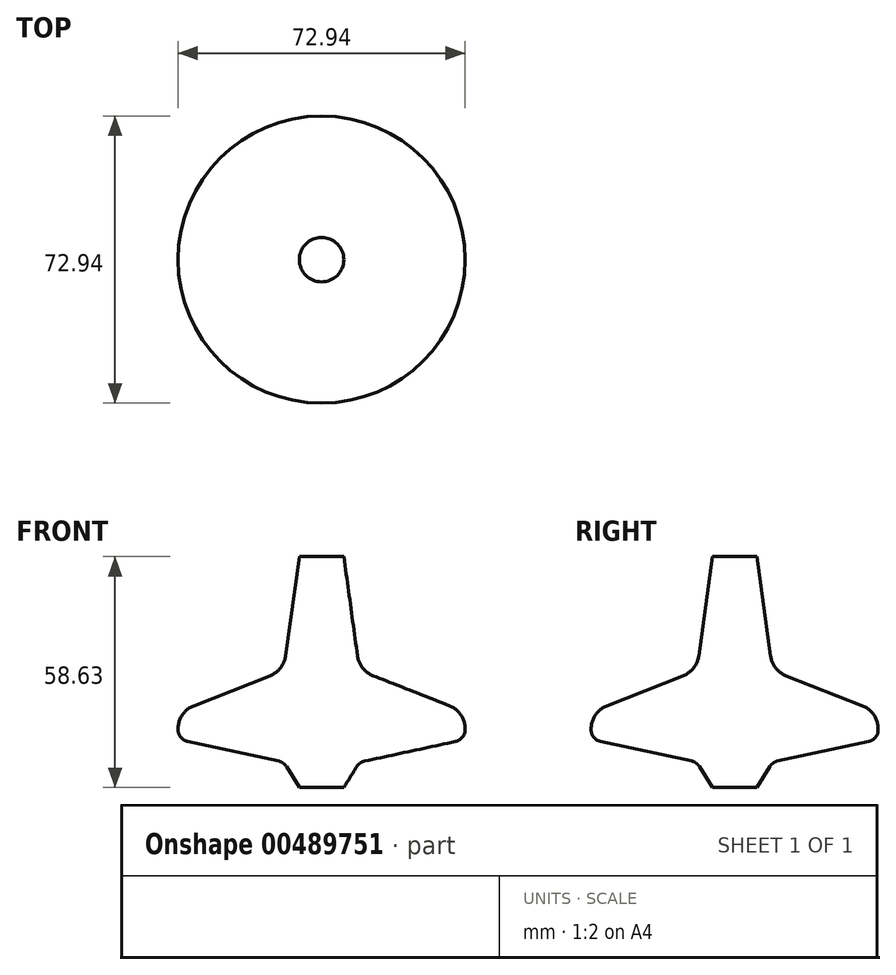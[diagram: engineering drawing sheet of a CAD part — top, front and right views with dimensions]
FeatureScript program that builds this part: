
annotation { "Feature Type Name" : "Feature", "Feature Type Description" : "" }
export const myFeature = defineFeature(function(context is Context, id is Id, definition is map)
    precondition{}
    {
        {
            var Q0;
            Q0=qCreatedBy(makeId("Front.planeOp"),FACE);
            var sketch = newSketch(context, id + "F0", { "sketchPlane" : qUnion([Q0])});
            skLineSegment(sketch, "E0", {"start": v(0, 0) * mm, "end": v(5.66, 0) * mm});
            skLineSegment(sketch, "E1", {"start": v(5.66, 0) * mm, "end": v(8.95, 5.3) * mm});
            skLineSegment(sketch, "E2", {"start": v(10.9, 6.68) * mm, "end": v(34.05, 11.67) * mm});
            skLineSegment(sketch, "E3", {"start": v(36.47, 14.66) * mm, "end": v(36.47, 14.86) * mm});
            skLineSegment(sketch, "E4", {"start": v(32.44, 20.77) * mm, "end": v(13.1, 28.4) * mm});
            skLineSegment(sketch, "E5", {"start": v(9.13, 33.43) * mm, "end": v(5.66, 58.63) * mm});
            skLineSegment(sketch, "E6", {"start": v(5.66, 58.63) * mm, "end": v(0, 58.63) * mm});
            skLineSegment(sketch, "E7", {"start": v(0, 58.63) * mm, "end": v(0, 0) * mm});
            skPoint(sketch, "E8.visualSharp", {"position": v(9.63, 29.75) * mm});
            skArc(sketch, "E8.filletArc", {"start": v(9.13, 33.43) * mm, "mid": v(10.43, 30.37) * mm, "end": v(13.1, 28.4) * mm});
            skPoint(sketch, "E9.visualSharp", {"position": v(36.47, 19.19) * mm});
            skArc(sketch, "E9.filletArc", {"start": v(36.47, 14.86) * mm, "mid": v(35.37, 18.44) * mm, "end": v(32.44, 20.77) * mm});
            skPoint(sketch, "E10.visualSharp", {"position": v(36.47, 12.2) * mm});
            skArc(sketch, "E10.filletArc", {"start": v(34.05, 11.67) * mm, "mid": v(35.79, 12.74) * mm, "end": v(36.47, 14.66) * mm});
            skPoint(sketch, "E11.visualSharp", {"position": v(9.63, 6.4) * mm});
            skArc(sketch, "E11.filletArc", {"start": v(10.9, 6.68) * mm, "mid": v(9.79, 6.19) * mm, "end": v(8.95, 5.3) * mm});
            skSolve(sketch);
        }
        {
            var Q0;
            Q0=makeQuery(id+"F0.imprint","IMPRINT",FACE,{"disambiguationData":[TD([[makeQuery(id+"F0.imprint","IMPRINT",EDGE,{"derivedFrom":sQuery(id+"F0.wireOp",EDGE,"E0")}),1.0]])]});
            var Q1;
            Q1=sQuery(id+"F0.wireOp",EDGE,"E7");
            revolve(context, id + "F1", {"entities" : qUnion([Q0]), "axis" : qUnion([Q1]), "revolveType" : RevolveType.FULL});
        }
    });
